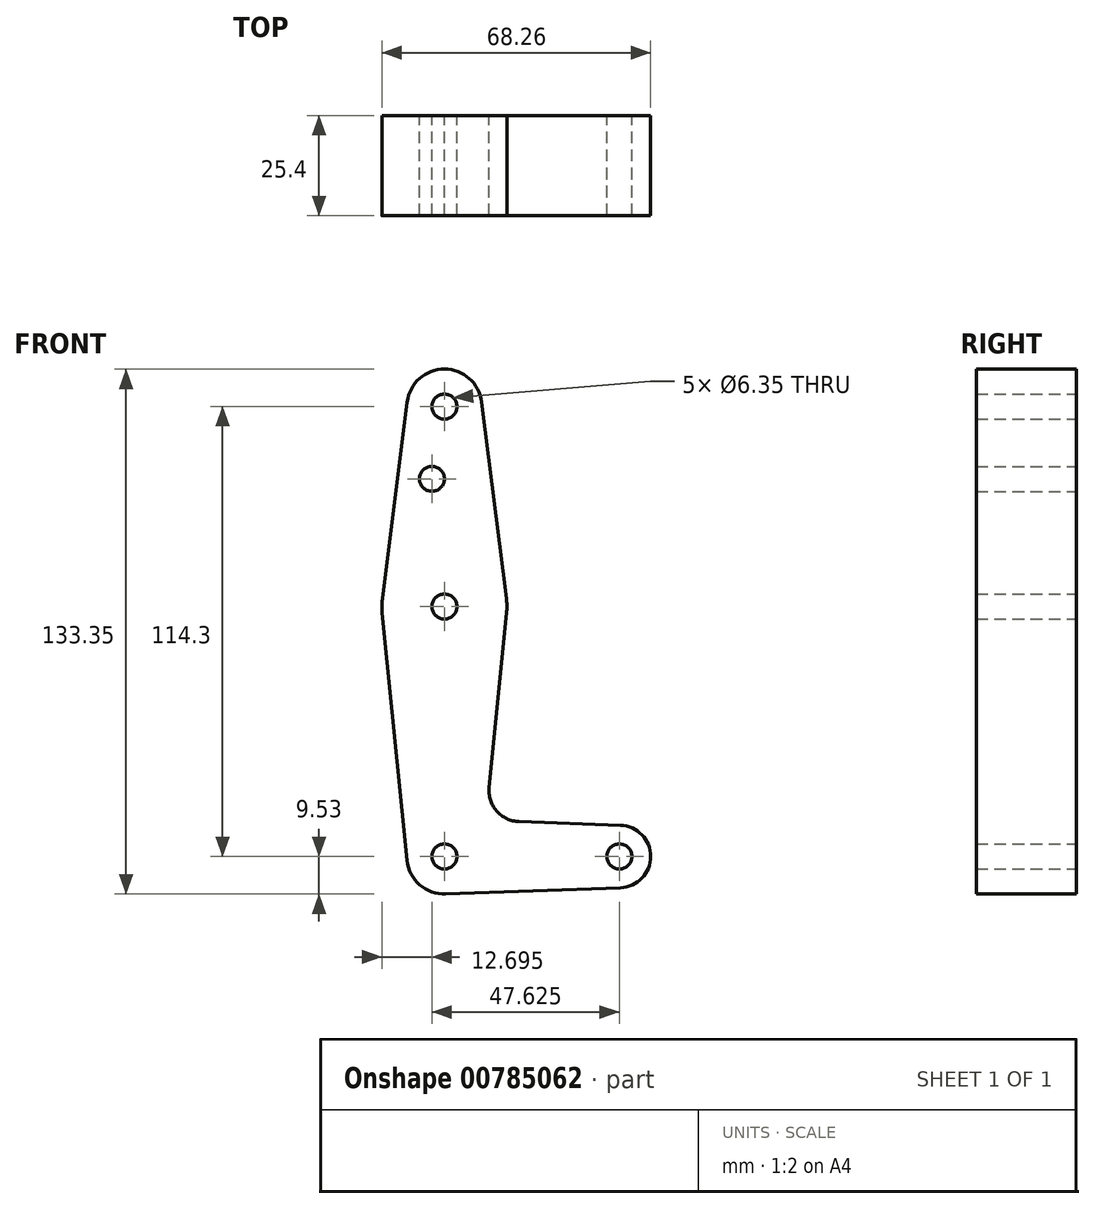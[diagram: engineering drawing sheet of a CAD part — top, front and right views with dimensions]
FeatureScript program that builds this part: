
annotation { "Feature Type Name" : "Feature", "Feature Type Description" : "" }
export const myFeature = defineFeature(function(context is Context, id is Id, definition is map)
    precondition{}
    {
        {
            var Q0;
            Q0=qCreatedBy(makeId("Front.planeOp"),FACE);
            var sketch = newSketch(context, id + "F0", { "sketchPlane" : qUnion([Q0])});
            skLineSegment(sketch, "E0", {"start": v(0, 50.8) * mm, "end": v(0, -63.5) * mm});
            skLineSegment(sketch, "E1", {"start": v(0, -63.5) * mm, "end": v(44.45, -63.5) * mm});
            skCircle(sketch, "E2", {"center": v(0, 0) * mm, "radius": 15.88 * mm});
            skCircle(sketch, "E3", {"center": v(0, 50.8) * mm, "radius": 9.53 * mm});
            skCircle(sketch, "E4", {"center": v(44.45, -63.5) * mm, "radius": 7.94 * mm});
            skLineSegment(sketch, "E5", {"start": v(-9.45, 52) * mm, "end": v(-15.75, 1.98) * mm});
            skLineSegment(sketch, "E6", {"start": v(0, -73.03) * mm, "end": v(44.73, -71.43) * mm});
            skLineSegment(sketch, "E7", {"start": v(18.97, -54.65) * mm, "end": v(44.73, -55.57) * mm});
            skLineSegment(sketch, "E8", {"start": v(15.8, -1.59) * mm, "end": v(11.34, -45.9) * mm});
            skLineSegment(sketch, "E9", {"start": v(-15.8, -1.59) * mm, "end": v(-9.48, -64.45) * mm});
            skLineSegment(sketch, "E10", {"start": v(9.45, 52) * mm, "end": v(15.75, 1.98) * mm});
            skCircle(sketch, "E11", {"center": v(0, 0) * mm, "radius": 3.18 * mm});
            skCircle(sketch, "E12", {"center": v(-3.17, 32.45) * mm, "radius": 3.18 * mm});
            skCircle(sketch, "E13", {"center": v(0, -63.5) * mm, "radius": 3.18 * mm});
            skCircle(sketch, "E14", {"center": v(0, 50.8) * mm, "radius": 3.18 * mm});
            skCircle(sketch, "E15", {"center": v(44.45, -63.5) * mm, "radius": 3.18 * mm});
            skArc(sketch, "E16.filletArc", {"start": v(11.34, -45.9) * mm, "mid": v(13.26, -51.93) * mm, "end": v(18.97, -54.65) * mm});
            skCircle(sketch, "E17", {"center": v(0, -63.5) * mm, "radius": 9.53 * mm});
            skSolve(sketch);
        }
        {
            var Q0;
            Q0 = qSketchRegion(id + "F0", true);
            var Q1;
            {var subQ0=sQuery(id+"F0.wireOp",EDGE,"E17");var subQ1=sQuery(id+"F0.wireOp",EDGE,"E0");var subQ2=makeQuery(id+"F0.imprint","INTERSECT",VERTEX,{"derivedFrom":[subQ1,subQ0]});Q1=makeQuery(id+"F0.imprint","IMPRINT",FACE,{"disambiguationData":[TD([[makeQuery(id+"F0.imprint","IMPRINT",EDGE,{"disambiguationData":[TD([[subQ2,-1.0]])],"derivedFrom":subQ1}),1.0]])]});}
            extrude(context, id + "F1", {"entities" : qUnion([Q0, Q1]), "depth" : 25.4 * mm, "offsetDistance" : 25.4 * mm});
        }
    });
